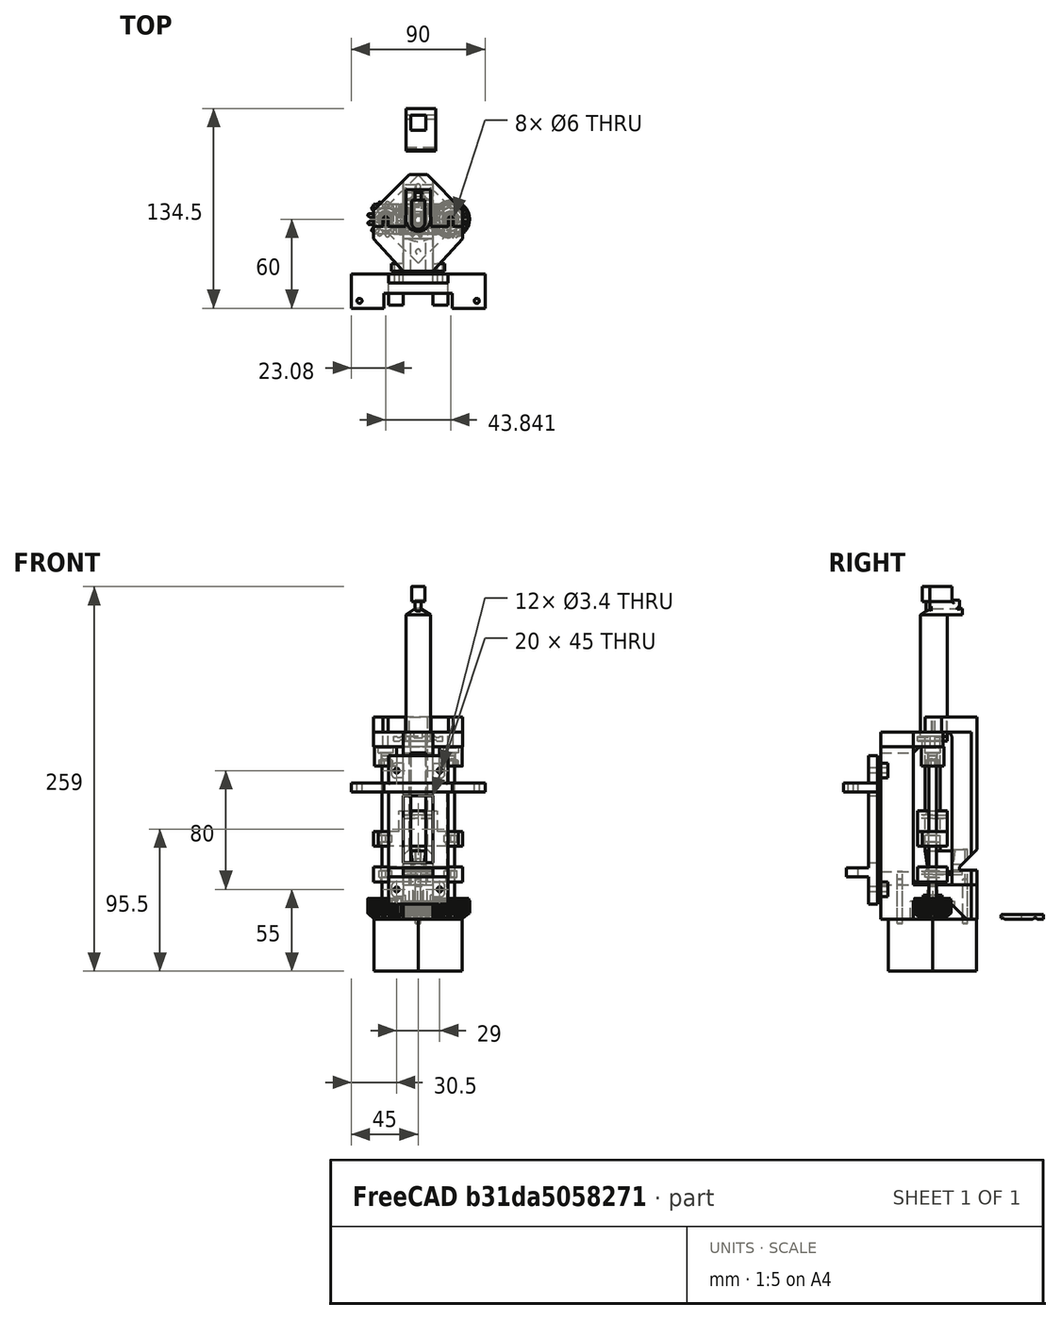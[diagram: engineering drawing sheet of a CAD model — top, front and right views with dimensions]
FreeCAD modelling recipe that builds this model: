
FCSTD DOCUMENT  (FreeCAD 0.19R24291 (Git))
Label: syringe-pump
License: CC-BY 3.0
LicenseURL: http://creativecommons.org/licenses/by/3.0/
objects: Part::Cut×65, Part::Box×55, Part::Cylinder×53, Part::Fuse×40, Part::Fillet×20, Part::Chamfer×9, Part::Feature×8, Part::MultiCommon×7, App::DocumentObjectGroup×6, Part::MultiFuse×5, Part::Cone×4, Part::FeaturePython×4, Part::Wedge×3
note: 273 computed .brp shape members not serialized (recipe doc carries the construction recipe); baked Part::Feature solids carry a one-line shape summary decoded from their .brp

FEATURE [Part::Cylinder] Cylinder
  Angle = 360
  AttacherType = Attacher::AttachEngine3D
  Height = 22
  Radius = 2.6
FEATURE [Part::Box] Box  label="Cube"
  AttacherType = Attacher::AttachEngine3D
  Height = 30
  Length = 10
  Placement = pos=(-5,2,-1) rot=(0,0,1;0rad)
  Width = 10
FEATURE [Part::Cut] Cut  label="motor-shaft"
  Base = -> Cylinder
  Placement = pos=(0,0,0) rot=(0,0,1;0.785398rad)
  Tool = -> Box
FEATURE [Part::Cylinder] Cylinder001  label="screw1"
  Angle = 360
  AttacherType = Attacher::AttachEngine3D
  Height = 30
  Placement = pos=(-1e-15,21.9203,-3) rot=(0,0,1;0.785398rad)
  Radius = 1.7
FEATURE [Part::Cylinder] Cylinder002  label="drive-screw-2"
  Angle = 360
  AttacherType = Attacher::AttachEngine3D
  Height = 100
  Placement = pos=(-21.9203,-1e-15,10) rot=(0,0,1;0.785398rad)
  Radius = 2.5
FEATURE [Part::Cylinder] Cylinder003  label="screw3"
  Angle = 360
  AttacherType = Attacher::AttachEngine3D
  Height = 30
  Placement = pos=(1e-15,-21.9203,-3) rot=(0,0,1;0.785398rad)
  Radius = 1.7
FEATURE [Part::Cylinder] Cylinder004  label="drive-screw-1"
  Angle = 360
  AttacherType = Attacher::AttachEngine3D
  Height = 100
  Placement = pos=(21.9203,1e-15,10) rot=(0,0,1;0.785398rad)
  Radius = 2.5
FEATURE [Part::Feature] Part__Feature  label="paste-extruder-drive-gear-a"
  Placement = pos=(0,0,3) rot=(0,0,1;0rad)
  shape: bbox 24.94 x 25.13 x 8 mm, 389 faces (baked)
FEATURE [Part::Cylinder] Cylinder005  label="Cylinder001"
  Angle = 360
  AttacherType = Attacher::AttachEngine3D
  Height = 85
  Radius = 8.25
FEATURE [Part::Box] Box001  label="Cube001"
  AttacherType = Attacher::AttachEngine3D
  Height = 3
  Length = 20
  Placement = pos=(-8.25,-16.5,0) rot=(0,0,1;0rad)
  Width = 33
FEATURE [Part::Cone] Cone
  Angle = 360
  AttacherType = Attacher::AttachEngine3D
  Height = 4
  Placement = pos=(0,0,85) rot=(0,0,1;0rad)
  Radius1 = 8.25
  Radius2 = 2
FEATURE [Part::Cylinder] Cylinder006  label="Cylinder002"
  Angle = 360
  AttacherType = Attacher::AttachEngine3D
  Height = 10
  Placement = pos=(-2.3,0,94) rot=(0,0,1;0rad)
  Radius = 4.5
FEATURE [Part::Cylinder] Cylinder007  label="Cylinder003"
  Angle = 360
  AttacherType = Attacher::AttachEngine3D
  Height = 10
  Placement = pos=(-2.3,0,85) rot=(0,0,1;0rad)
  Radius = 2
FEATURE [Part::Cylinder] Cylinder008  label="Cylinder004"
  Angle = 360
  AttacherType = Attacher::AttachEngine3D
  Height = 24
  Placement = pos=(-10,11,-1.3) rot=(0,1,0;1.5708rad)
  Radius = 2
FEATURE [Part::Cylinder] Cylinder009  label="Cylinder005"
  Angle = 360
  AttacherType = Attacher::AttachEngine3D
  Height = 24
  Placement = pos=(-10,-11,-1.3) rot=(0,1,0;1.5708rad)
  Radius = 2
FEATURE [Part::Cylinder] Cylinder010  label="Cylinder006"
  Angle = 360
  AttacherType = Attacher::AttachEngine3D
  Height = 24
  Placement = pos=(-10,13,4.3) rot=(0,1,0;1.5708rad)
  Radius = 2
FEATURE [Part::Cylinder] Cylinder011  label="Cylinder007"
  Angle = 360
  AttacherType = Attacher::AttachEngine3D
  Height = 24
  Placement = pos=(-10,-13,4.3) rot=(0,1,0;1.5708rad)
  Radius = 2
FEATURE [Part::Cut] Cut001
  Base = -> Box001
  Tool = -> Cylinder008
FEATURE [Part::Cut] Cut002
  Base = -> Cut001
  Tool = -> Cylinder009
FEATURE [Part::Cut] Cut003
  Base = -> Cut002
  Tool = -> Cylinder011
FEATURE [Part::Cut] Cut004
  Base = -> Cut003
  Placement = pos=(-2,0,0) rot=(0,0,1;0rad)
  Tool = -> Cylinder010
FEATURE [Part::Fuse] Fusion
  Base = -> Cylinder005
  Tool = -> Cut004
FEATURE [Part::Fuse] Fusion001
  Base = -> Cylinder007
  Tool = -> Fusion
FEATURE [Part::Fuse] Fusion002  label="syringe-1"
  Base = -> Cylinder006
  Tool = -> Fusion001
FEATURE [Part::Fuse] Fusion003
  Base = -> Cone
  Tool = -> Fusion002
FEATURE [Part::Box] Box002  label="Cube002"
  AttacherType = Attacher::AttachEngine3D
  Height = 80
  Length = 10
  Placement = pos=(-5,-5,16) rot=(0,0,1;0rad)
  Width = 10
FEATURE [Part::Wedge] Wedge
  AttacherType = Attacher::AttachEngine3D
  Placement = pos=(-5,-5,16) rot=(-1,0,0;1.5708rad)
  X2max = 18
  X2min = 2
  Xmax = 20
  Xmin = 0
  Ymax = 14
  Ymin = 0
  Z2max = 8
  Z2min = 2
  Zmax = 10
  Zmin = 0
FEATURE [Part::Cylinder] Cylinder012  label="Cylinder008"
  Angle = 360
  AttacherType = Attacher::AttachEngine3D
  Height = 2
  Radius = 9.5
FEATURE [Part::Fuse] Fusion004
  Base = -> Box002
  Tool = -> Wedge
FEATURE [Part::Fuse] Fusion005
  Base = -> Cylinder012
  Tool = -> Fusion004
FEATURE [Part::Box] Box003  label="motor-body"
  AttacherType = Attacher::AttachEngine3D
  Height = 35
  Length = 42
  Placement = pos=(2e-15,-29.6985,-35) rot=(0,0,1;0.785398rad)
  Width = 42
FEATURE [Part::Box] Box004  label="Cube003"
  AttacherType = Attacher::AttachEngine3D
  Height = 2
  Length = 20
  Placement = pos=(0,-9.5,0) rot=(0,0,1;0rad)
  Width = 19
FEATURE [Part::Fuse] Fusion006
  Base = -> Fusion005
  Tool = -> Box004
FEATURE [Part::Fillet] Fillet001
  Base = -> Fusion006
  Edges = 3 edges r=3: [Edge9,Edge20,Edge24]
FEATURE [Part::Fillet] Fillet002
  Base = -> Fillet001
  Edges = 3 edges r=3: [Edge8,Edge27,Edge29]
FEATURE [Part::Fillet] Fillet003  label="piston"
  Base = -> Fillet002
  Edges = 3 edges r=3: [Edge33,Edge34,Edge36]
  Placement = pos=(0,0,30) rot=(0,0,1;0.785398rad)
FEATURE [Part::Box] Box005  label="Cube004"
  AttacherType = Attacher::AttachEngine3D
  Height = 85
  Length = 10
  Placement = pos=(0,-8.25,0) rot=(0,0,1;0rad)
  Width = 16.5
FEATURE [Part::Fuse] Fusion007
  Base = -> Fusion003
  Tool = -> Box005
FEATURE [Part::Wedge] Wedge003
  AttacherType = Attacher::AttachEngine3D
  Placement = pos=(0,8.25,85) rot=(1,0,0;1.5708rad)
  X2max = 20
  X2min = 0
  Xmax = 20
  Xmin = 0
  Ymax = 4
  Ymin = 0
  Z2max = 10.25
  Z2min = 6.25
  Zmax = 16.5
  Zmin = 0
FEATURE [Part::Fuse] Fusion008
  Base = -> Fusion007
  Tool = -> Wedge003
FEATURE [Part::Box] Box006  label="Cube005"
  AttacherType = Attacher::AttachEngine3D
  Height = 10
  Length = 20
  Placement = pos=(-2,-2,85) rot=(0,0,1;0rad)
  Width = 4
FEATURE [Part::Fuse] Fusion009
  Base = -> Fusion008
  Tool = -> Box006
FEATURE [Part::Box] Box007  label="Cube006"
  AttacherType = Attacher::AttachEngine3D
  Height = 10
  Length = 15
  Placement = pos=(-2,-4.5,94) rot=(0,0,1;0rad)
  Width = 9
FEATURE [Part::Fuse] Fusion010
  Base = -> Fusion009
  Tool = -> Box007
FEATURE [Part::Fillet] Fillet  label="syringe-body"
  Base = -> Fusion010
  Edges = 5 edges r=1.5: [Edge23,Edge27,Edge33,Edge38,Edge58]
  Placement = pos=(0,0,120) rot=(0,0,1;1.5708rad)
FEATURE [Part::Box] Box008  label="Cube007"
  AttacherType = Attacher::AttachEngine3D
  Height = 10
  Length = 20
  Placement = pos=(14.1421,-28.2843,25) rot=(0,0,1;0.785398rad)
  Width = 60
FEATURE [Part::Cut] Cut005
  Base = -> Box008
  Tool = -> Fillet003
FEATURE [Part::Fillet] Fillet004
  Base = -> Fillet001
  Edges = 3 edges r=3: [Edge8,Edge27,Edge29]
FEATURE [Part::Fillet] Fillet005  label="piston001"
  Base = -> Fillet004
  Edges = 3 edges r=3: [Edge33,Edge34,Edge36]
  Placement = pos=(0,0,30) rot=(0,0,1;1.5708rad)
FEATURE [App::DocumentObjectGroup] Group001  label="syringe"
  Group = -> [Fillet003,Fillet,Fillet005]
FEATURE [Part::Cylinder] Cylinder017  label="drive-screw-003"
  Angle = 360
  AttacherType = Attacher::AttachEngine3D
  Height = 100
  Placement = pos=(15.5,-15.5,10) rot=(0,0,1;0rad)
  Radius = 3
FEATURE [Part::Cylinder] Cylinder018  label="drive-screw-004"
  Angle = 360
  AttacherType = Attacher::AttachEngine3D
  Height = 100
  Placement = pos=(-15.5,15.5,10) rot=(0,0,1;0rad)
  Radius = 3
FEATURE [Part::Cut] Cut006
  Base = -> Cut005
  Tool = -> Cylinder017
FEATURE [Part::Cut] Cut007
  Base = -> Cut006
  Tool = -> Cylinder018
FEATURE [Part::Box] Box009  label="Cube008"
  AttacherType = Attacher::AttachEngine3D
  Height = 4.5
  Length = 20
  Placement = pos=(0,-4.25,0) rot=(0,0,1;0rad)
  Width = 8.5
FEATURE [Part::Box] Box010  label="Cube009"
  AttacherType = Attacher::AttachEngine3D
  Height = 8
  Length = 20
  Placement = pos=(0,0,-1) rot=(0,0,1;1.0472rad)
  Width = 8.5
FEATURE [Part::Box] Box011  label="Cube010"
  AttacherType = Attacher::AttachEngine3D
  Height = 8
  Length = 20
  Placement = pos=(0,0,-1) rot=(0,0,1;3.66519rad)
  Width = 8.5
FEATURE [Part::Cut] Cut008
  Base = -> Box009
  Tool = -> Box010
FEATURE [Part::Cut] Cut009
  Base = -> Cut008
  Placement = pos=(11.965,-19.035,28) rot=(0,0,1;0.785398rad)
  Tool = -> Box011
FEATURE [Part::Box] Box012  label="Cube011"
  AttacherType = Attacher::AttachEngine3D
  Height = 8
  Length = 20
  Placement = pos=(0,0,-1) rot=(0,0,1;3.66519rad)
  Width = 8.5
FEATURE [Part::Cut] Cut011
  Base = -> Box009
  Tool = -> Box010
FEATURE [Part::Cut] Cut010
  Base = -> Cut011
  Placement = pos=(-19.035,11.965,28) rot=(0,0,1;0.785398rad)
  Tool = -> Box012
FEATURE [Part::Cut] Cut012
  Base = -> Cut007
  Tool = -> Cut009
FEATURE [Part::Cut] Cut013  label="paste-extruder-drive-blockaa"
  Base = -> Cut012
  Placement = pos=(0,0,0) rot=(0,0,1;0.785398rad)
  Tool = -> Cut010
FEATURE [Part::Feature] Part__Feature001  label="paste-extruder-driven-gear-a"
  Placement = pos=(21.9203,0,3) rot=(0,0,1;0rad)
  shape: bbox 25.3 x 25.3 x 13 mm, 290 faces (baked)
FEATURE [Part::Feature] Part__Feature003  label="Z Driven Gear002"
  shape: bbox 25.3 x 25.3 x 13 mm, 290 faces (baked)
FEATURE [Part::Cylinder] Cylinder019  label="Cylinder009"
  Angle = 360
  AttacherType = Attacher::AttachEngine3D
  Height = 20
  Placement = pos=(0,0,-4) rot=(0,0,1;0rad)
  Radius = 7.5
FEATURE [Part::MultiCommon] Common  label="paste-extruder-bearing-holder-a"
  Placement = pos=(21.9203,1e-15,113) rot=(0.92388,0.382683,0;3.14159rad)
  Shapes = -> [Part__Feature003,Cylinder019]
FEATURE [Part::Feature] Part__Feature004  label="Z Driven Gear003"
  shape: bbox 25.3 x 25.3 x 13 mm, 290 faces (baked)
FEATURE [Part::Cylinder] Cylinder020  label="Cylinder010"
  Angle = 360
  AttacherType = Attacher::AttachEngine3D
  Height = 20
  Placement = pos=(0,0,-4) rot=(0,0,1;0rad)
  Radius = 7.5
FEATURE [Part::MultiCommon] Common001  label="paste-extruder-bearing-holder-b"
  Placement = pos=(-21.9203,-1e-15,113) rot=(0.92388,0.382683,0;3.14159rad)
  Shapes = -> [Part__Feature004,Cylinder020]
FEATURE [App::DocumentObjectGroup] Group002  label="Hardware"
  Group = -> [Box003,Cylinder003,Cylinder001,Cylinder004,Cylinder002,Cut]
FEATURE [Part::Box] Box013  label="Cube012"
  AttacherType = Attacher::AttachEngine3D
  Height = 10
  Length = 20
  Placement = pos=(30,-13,116) rot=(0,0,1;1.5708rad)
  Width = 60
FEATURE [Part::Box] Box014  label="Cube013"
  AttacherType = Attacher::AttachEngine3D
  Height = 146
  Length = 20
  Placement = pos=(-10,-35,-20) rot=(0,0,1;0rad)
  Width = 22
FEATURE [Part::Cylinder] Cylinder021  label="Cylinder011"
  Angle = 360
  AttacherType = Attacher::AttachEngine3D
  Height = 12
  Radius = 15
FEATURE [Part::Box] Box016  label="motor-body001"
  AttacherType = Attacher::AttachEngine3D
  Height = 35
  Length = 82
  Placement = pos=(0,-49.6985,-35) rot=(0,0,1;0.785398rad)
  Width = 82
FEATURE [Part::Cylinder] Cylinder022  label="screw004"
  Angle = 360
  AttacherType = Attacher::AttachEngine3D
  Height = 60
  Placement = pos=(0,-21.9203,-3) rot=(0,0,1;0.785398rad)
  Radius = 1.7
FEATURE [Part::Box] Box017  label="Cube015"
  AttacherType = Attacher::AttachEngine3D
  Height = 10
  Length = 20
  Placement = pos=(-10,-35,116) rot=(0,0,1;0.737402rad)
  Width = 29.74
FEATURE [Part::Box] Box018  label="Cube016"
  AttacherType = Attacher::AttachEngine3D
  Height = 10
  Length = 29.74
  Placement = pos=(10,-35,116) rot=(0,0,1;0.833395rad)
  Width = 20
FEATURE [Part::Fuse] Fusion014
  Base = -> Fusion009
  Tool = -> Box007
FEATURE [Part::Fillet] Fillet006  label="syringe-body001"
  Base = -> Fusion014
  Edges = 5 edges r=1.5: [Edge23,Edge27,Edge33,Edge38,Edge58]
  Placement = pos=(0,0,120) rot=(0,0,1;1.5708rad)
FEATURE [Part::Box] Box019  label="Cube017"
  AttacherType = Attacher::AttachEngine3D
  Height = 10
  Length = 12
  Placement = pos=(-6,-7,111) rot=(0,0,1;0rad)
  Width = 20
FEATURE [Part::Cylinder] Cylinder023  label="drive-screw-005"
  Angle = 360
  AttacherType = Attacher::AttachEngine3D
  Height = 100
  Placement = pos=(21.9203,0,50) rot=(0,0,1;0.785398rad)
  Radius = 1.7
FEATURE [Part::Cylinder] Cylinder024  label="drive-screw-006"
  Angle = 360
  AttacherType = Attacher::AttachEngine3D
  Height = 100
  Placement = pos=(-21.9203,0,50) rot=(0,0,1;0.785398rad)
  Radius = 1.7
FEATURE [Part::Box] Box020  label="Cube018"
  AttacherType = Attacher::AttachEngine3D
  Height = 10
  Length = 10
  Placement = pos=(8,-35,15) rot=(0,0,1;0rad)
  Width = 5
FEATURE [Part::Cylinder] Cylinder025  label="Cylinder012"
  Angle = 360
  AttacherType = Attacher::AttachEngine3D
  Height = 50
  Placement = pos=(14.5,-15,20) rot=(1,0,0;1.5708rad)
  Radius = 1.7
FEATURE [Part::Cut] Cut022
  Base = -> Box020
  Tool = -> Cylinder025
FEATURE [Part::Fillet] Fillet007
  Base = -> Cut022
  Edges = 1 edges r=3: [Edge14]
FEATURE [Part::Fillet] Fillet008  label="tab"
  Base = -> Fillet007
  Edges = 1 edges r=3: [Edge14]
FEATURE [Part::Fillet] Fillet009
  Base = -> Cut022
  Edges = 1 edges r=3: [Edge14]
FEATURE [Part::Fillet] Fillet010  label="tab001"
  Base = -> Fillet009
  Edges = 1 edges r=3: [Edge14]
  Placement = pos=(0,0,80) rot=(0,0,1;0rad)
FEATURE [Part::Fillet] Fillet011
  Base = -> Cut022
  Edges = 1 edges r=3: [Edge14]
FEATURE [Part::Fillet] Fillet012  label="tab002"
  Base = -> Fillet011
  Edges = 1 edges r=3: [Edge14]
  Placement = pos=(0,0,40) rot=(0,1,0;3.14159rad)
FEATURE [Part::Fillet] Fillet013
  Base = -> Cut022
  Edges = 1 edges r=3: [Edge14]
FEATURE [Part::Fillet] Fillet014  label="tab003"
  Base = -> Fillet013
  Edges = 1 edges r=3: [Edge14]
  Placement = pos=(0,0,120) rot=(0,1,0;3.14159rad)
FEATURE [Part::Box] Box021  label="body-slot"
  AttacherType = Attacher::AttachEngine3D
  Height = 89
  Length = 10
  Placement = pos=(-5,-40,23) rot=(0,0,1;0rad)
  Width = 80
FEATURE [Part::Box] Box022  label="Cube019"
  AttacherType = Attacher::AttachEngine3D
  Height = 23
  Length = 20
  Placement = pos=(-10,-35,0) rot=(0,0,1;0rad)
  Width = 65
FEATURE [Part::Box] Box023  label="Cube020"
  AttacherType = Attacher::AttachEngine3D
  Height = 20
  Length = 30
  Placement = pos=(-15,10,13) rot=(-1,0,0;0.785398rad)
  Width = 65
FEATURE [Part::Box] Box024  label="Cube021"
  AttacherType = Attacher::AttachEngine3D
  Height = 20
  Length = 30
  Placement = pos=(-15,-37,12) rot=(0,0,1;0rad)
  Width = 70
FEATURE [Part::Fuse] Fusion015
  Base = -> Box023
  Tool = -> Box024
FEATURE [Part::MultiCommon] Common002
  Shapes = -> [Box022,Fusion015]
FEATURE [Part::Fuse] Fusion016
  Base = -> Box014
  Tool = -> Common002
FEATURE [Part::Chamfer] Chamfer
  Base = -> Fusion016
  Edges = 1 edges r=4: [Edge27]
FEATURE [Part::Chamfer] Chamfer001
  Base = -> Chamfer
  Edges = 1 edges r=4: [Edge26]
FEATURE [Part::Cut] Cut023
  Base = -> Chamfer001
  Tool = -> Cylinder021
FEATURE [Part::Cut] Cut024
  Base = -> Cut023
  Tool = -> Cylinder022
FEATURE [Part::Cut] Cut025
  Base = -> Cut024
  Tool = -> Box016
FEATURE [Part::Cylinder] Cylinder026  label="screw005"
  Angle = 360
  AttacherType = Attacher::AttachEngine3D
  Height = 56
  Placement = pos=(0,21.9203,-3) rot=(0,0,1;0.785398rad)
  Radius = 1.7
FEATURE [Part::Cut] Cut026
  Base = -> Cut025
  Tool = -> Cylinder026
FEATURE [Part::Fuse] Fusion017
  Base = -> Box013
  Tool = -> Box018
FEATURE [Part::Fuse] Fusion018
  Base = -> Box017
  Tool = -> Fusion017
FEATURE [Part::Fuse] Fusion019
  Base = -> Cut026
  Tool = -> Fusion018
FEATURE [Part::Fuse] Fusion020
  Base = -> Fillet008
  Tool = -> Fusion019
FEATURE [Part::Fuse] Fusion021
  Base = -> Fillet014
  Tool = -> Fusion020
FEATURE [Part::Fuse] Fusion022
  Base = -> Fillet012
  Tool = -> Fusion021
FEATURE [Part::Fuse] Fusion023
  Base = -> Fillet010
  Tool = -> Fusion022
FEATURE [Part::Cut] Cut027
  Base = -> Fusion023
  Tool = -> Fillet006
FEATURE [Part::Cut] Cut028
  Base = -> Cut027
  Tool = -> Box019
FEATURE [Part::Cut] Cut029
  Base = -> Cut028
  Tool = -> Cylinder024
FEATURE [Part::Cut] Cut030
  Base = -> Cut029
  Tool = -> Cylinder023
FEATURE [Part::Cut] Cut031
  Base = -> Cut030
  Tool = -> Box021
FEATURE [Part::Cylinder] Cylinder027  label="drive-screw-007"
  Angle = 360
  AttacherType = Attacher::AttachEngine3D
  Height = 10
  Placement = pos=(21.9203,0,6) rot=(0,0,1;0.785398rad)
  Radius = 13.5
FEATURE [Part::Cylinder] Cylinder028  label="drive-screw-008"
  Angle = 360
  AttacherType = Attacher::AttachEngine3D
  Height = 10
  Placement = pos=(-21.9203,0,6) rot=(0,0,1;0.785398rad)
  Radius = 13.5
FEATURE [Part::Cut] Cut032
  Base = -> Cut031
  Tool = -> Cylinder027
FEATURE [Part::Cut] Cut033  label="frame-1"
  Base = -> Cut032
  Tool = -> Cylinder028
FEATURE [Part::Cylinder] Cylinder029  label="Cylinder013"
  Angle = 360
  AttacherType = Attacher::AttachEngine3D
  Height = 50
  Radius = 3.5
FEATURE [Part::Cut] Cut034  label="old-frame"
  Base = -> Cut033
  Tool = -> Cylinder029
FEATURE [Part::FeaturePython] Clone  label="paste-extruder-bearing-holder-1"  # Draft clone (typed FeaturePython)
  Objects = -> [Common]
  Placement = pos=(21.3,0,113) rot=(0.92388,0.382683,0;3.14159rad)
  Scale = (1.03,1.03,1)
FEATURE [Part::Cylinder] Cylinder030  label="mounting hole"
  Angle = 360
  AttacherType = Attacher::AttachEngine3D
  Height = 50
  Placement = pos=(-14.5,0,20) rot=(1,0,0;1.5708rad)
  Radius = 1.7
FEATURE [Part::Cylinder] Cylinder031  label="mounting hole001"
  Angle = 360
  AttacherType = Attacher::AttachEngine3D
  Height = 50
  Placement = pos=(14.5,0,20) rot=(1,0,0;1.5708rad)
  Radius = 1.7
FEATURE [Part::Cylinder] Cylinder032  label="mounting hole002"
  Angle = 360
  AttacherType = Attacher::AttachEngine3D
  Height = 50
  Placement = pos=(-14.5,0,100) rot=(1,0,0;1.5708rad)
  Radius = 1.7
FEATURE [Part::Cylinder] Cylinder033  label="mounting hole003"
  Angle = 360
  AttacherType = Attacher::AttachEngine3D
  Height = 50
  Placement = pos=(14.5,0,100) rot=(1,0,0;1.5708rad)
  Radius = 1.7
FEATURE [Part::Box] Box025  label="Cube022"
  AttacherType = Attacher::AttachEngine3D
  Height = 100
  Length = 40
  Placement = pos=(-20,-41,10) rot=(0,0,1;0rad)
  Width = 6
FEATURE [Part::Box] Box026  label="Cube023"
  AttacherType = Attacher::AttachEngine3D
  Height = 6
  Length = 90
  Placement = pos=(-45,-58,85.5) rot=(0,0,1;0rad)
  Width = 23
FEATURE [Part::Box] Box027  label="Cube024"
  AttacherType = Attacher::AttachEngine3D
  Height = 6
  Length = 40
  Placement = pos=(-20,-56,28.5) rot=(0,0,1;0rad)
  Width = 15
FEATURE [Part::Cylinder] Cylinder034  label="mounting hole004"
  Angle = 360
  AttacherType = Attacher::AttachEngine3D
  Height = 50
  Placement = pos=(-39.5,-53,58) rot=(0,0,1;0rad)
  Radius = 1.7
FEATURE [Part::Cylinder] Cylinder035  label="mounting hole005"
  Angle = 360
  AttacherType = Attacher::AttachEngine3D
  Height = 50
  Placement = pos=(39.5,-53,58) rot=(0,0,1;0rad)
  Radius = 1.7
FEATURE [Part::Box] Box028  label="Cube025"
  AttacherType = Attacher::AttachEngine3D
  Height = 45
  Length = 20
  Placement = pos=(-10,-51,38) rot=(0,0,1;0rad)
  Width = 20
FEATURE [Part::Box] Box029  label="Cube026"
  AttacherType = Attacher::AttachEngine3D
  Height = 45
  Length = 20
  Placement = pos=(-10,-68,20) rot=(0,0,1;0rad)
  Width = 20
FEATURE [Part::Box] Box030  label="Cube027"
  AttacherType = Attacher::AttachEngine3D
  Height = 45
  Length = 46
  Placement = pos=(-23,-68,56) rot=(0,0,1;0rad)
  Width = 20
FEATURE [Part::Fuse] Fusion024
  Base = -> Box025
  Tool = -> Box026
FEATURE [Part::Fuse] Fusion025
  Base = -> Box027
  Tool = -> Fusion024
FEATURE [Part::Cut] Cut035
  Base = -> Fusion025
  Tool = -> Cylinder035
FEATURE [Part::Cut] Cut036
  Base = -> Cut035
  Tool = -> Cylinder034
FEATURE [Part::Cut] Cut037
  Base = -> Cut036
  Tool = -> Cylinder033
FEATURE [Part::Cut] Cut038
  Base = -> Cut037
  Tool = -> Cylinder032
FEATURE [Part::Cut] Cut039
  Base = -> Cut038
  Tool = -> Cylinder031
FEATURE [Part::Cut] Cut040
  Base = -> Cut039
  Tool = -> Cylinder030
FEATURE [Part::Cut] Cut041
  Base = -> Cut040
  Tool = -> Box030
FEATURE [Part::Cut] Cut042
  Base = -> Cut041
  Tool = -> Box029
FEATURE [Part::Cut] Cut043  label="paste-extruder-PSU-mounting-bracket"
  Base = -> Cut042
  Placement = pos=(0,-2,0) rot=(0,0,1;0rad)
  Tool = -> Box028
FEATURE [Part::Cylinder] Cylinder036  label="drive-screw-009"
  Angle = 360
  AttacherType = Attacher::AttachEngine3D
  Height = 100
  Placement = pos=(21.9203,0,50) rot=(0,0,1;0.785398rad)
  Radius = 1.7
FEATURE [Part::Cut] Cut044
  Base = -> Cut028
  Tool = -> Cylinder024
FEATURE [Part::Cut] Cut045
  Base = -> Cut044
  Tool = -> Cylinder036
FEATURE [Part::Box] Box031  label="body-slot001"
  AttacherType = Attacher::AttachEngine3D
  Height = 80
  Length = 10
  Placement = pos=(-5,-40,32) rot=(0,0,1;0rad)
  Width = 80
FEATURE [Part::Cylinder] Cylinder037  label="drive-screw-010"
  Angle = 360
  AttacherType = Attacher::AttachEngine3D
  Height = 10
  Placement = pos=(21.9203,0,6) rot=(0,0,1;0.785398rad)
  Radius = 13.5
FEATURE [Part::Cylinder] Cylinder038  label="drive-screw-011"
  Angle = 360
  AttacherType = Attacher::AttachEngine3D
  Height = 10
  Placement = pos=(-21.9203,0,6) rot=(0,0,1;0.785398rad)
  Radius = 13.5
FEATURE [Part::Cylinder] Cylinder039  label="Cylinder014"
  Angle = 360
  AttacherType = Attacher::AttachEngine3D
  Height = 50
  Radius = 3.5
FEATURE [Part::Fillet] Fillet015
  Base = -> Cut045
  Edges = 1 edges r=5: [Edge51]
FEATURE [Part::Cut] Cut046
  Base = -> Fillet015
  Tool = -> Box031
FEATURE [Part::Box] Box032  label="Cube028"
  AttacherType = Attacher::AttachEngine3D
  Height = 6
  Length = 20
  Placement = pos=(-10,-13,112) rot=(1,0,0;0.785398rad)
  Width = 6
FEATURE [Part::Fuse] Fusion026
  Base = -> Cut046
  Tool = -> Box032
FEATURE [Part::Cut] Cut047
  Base = -> Fusion026
  Tool = -> Cylinder039
FEATURE [Part::Cut] Cut048
  Base = -> Cut047
  Tool = -> Cylinder038
FEATURE [Part::Cut] Cut049  label="paste-extruder-frame"
  Base = -> Cut048
  Tool = -> Cylinder037
FEATURE [Part::Box] Box033  label="Cube029"
  AttacherType = Attacher::AttachEngine3D
  Height = 103
  Length = 20
  Placement = pos=(-10,13,23) rot=(0,0,1;0rad)
  Width = 17
FEATURE [Part::Box] Box034  label="Cube030"
  AttacherType = Attacher::AttachEngine3D
  Height = 10
  Length = 60
  Placement = pos=(-30,-5,126) rot=(0,0,1;0rad)
  Width = 35
FEATURE [Part::Box] Box035  label="Cube031"
  AttacherType = Attacher::AttachEngine3D
  Height = 122
  Length = 41
  Placement = pos=(-31,5,19) rot=(0,0,1;0.785398rad)
  Width = 17
FEATURE [Part::Box] Box036  label="Cube032"
  AttacherType = Attacher::AttachEngine3D
  Height = 124
  Length = 20
  Placement = pos=(33,3,19) rot=(0,0,1;0.785398rad)
  Width = 42
FEATURE [Part::Fuse] Fusion027
  Base = -> Box033
  Tool = -> Box034
FEATURE [Part::Cut] Cut050
  Base = -> Fusion027
  Tool = -> Box036
FEATURE [Part::Cut] Cut051
  Base = -> Cut050
  Tool = -> Box035
FEATURE [Part::Cylinder] Cylinder040  label="screw006"
  Angle = 360
  AttacherType = Attacher::AttachEngine3D
  Height = 56
  Placement = pos=(0,21.9203,-3) rot=(0,0,1;0.785398rad)
  Radius = 1.7
FEATURE [Part::Cylinder] Cylinder041  label="drive-screw-012"
  Angle = 360
  AttacherType = Attacher::AttachEngine3D
  Height = 100
  Placement = pos=(-21.9203,0,50) rot=(0,0,1;0.785398rad)
  Radius = 1.7
FEATURE [Part::Cylinder] Cylinder042  label="drive-screw-013"
  Angle = 360
  AttacherType = Attacher::AttachEngine3D
  Height = 100
  Placement = pos=(21.9203,0,50) rot=(0,0,1;0.785398rad)
  Radius = 1.7
FEATURE [Part::Box] Box037  label="Cube033"
  AttacherType = Attacher::AttachEngine3D
  Height = 56
  Length = 3.4
  Placement = pos=(-1.7,-2,-3) rot=(0,0,1;0rad)
  Width = 24
FEATURE [Part::Box] Box038  label="Cube034"
  AttacherType = Attacher::AttachEngine3D
  Height = 100
  Length = 3.4
  Placement = pos=(-23.7,-24,50) rot=(0,0,1;0rad)
  Width = 24
FEATURE [Part::Fuse] Fusion028  label="top-slot"
  Base = -> Cylinder040
  Placement = pos=(0,0,-6) rot=(0,0,1;0rad)
  Tool = -> Box037
FEATURE [Part::Box] Box039  label="Cube035"
  AttacherType = Attacher::AttachEngine3D
  Height = 100
  Length = 3.4
  Placement = pos=(20.3,-24,50) rot=(0,0,1;0rad)
  Width = 24
FEATURE [Part::Fuse] Fusion029  label="bottom-slot-1"
  Base = -> Cylinder042
  Tool = -> Box039
FEATURE [Part::Fuse] Fusion030  label="bottom-slot-2"
  Base = -> Cylinder041
  Tool = -> Box038
FEATURE [Part::Box] Box040  label="Cube036"
  AttacherType = Attacher::AttachEngine3D
  Height = 16
  Length = 22
  Placement = pos=(-11,18,33) rot=(0,0,1;0rad)
  Width = 17
FEATURE [Part::Box] Box041  label="Cube037"
  AttacherType = Attacher::AttachEngine3D
  Height = 16
  Length = 25
  Placement = pos=(-13,18,35) rot=(1,0,0;0.785398rad)
  Width = 32
FEATURE [Part::Cut] Cut052
  Base = -> Box040
  Tool = -> Box041
FEATURE [Part::Cut] Cut053
  Base = -> Cut051
  Tool = -> Cut052
FEATURE [Part::Cut] Cut054
  Base = -> Cut053
  Tool = -> Fusion028
FEATURE [Part::Cut] Cut055
  Base = -> Cut054
  Tool = -> Fusion030
FEATURE [Part::Cut] Cut056  label="top-strengthener1"
  Base = -> Cut055
  Tool = -> Fusion029
FEATURE [Part::Box] Box042  label="Cube038"
  AttacherType = Attacher::AttachEngine3D
  Height = 18
  Length = 17
  Placement = pos=(-8.5,-7,125) rot=(0,0,1;0rad)
  Width = 17
FEATURE [Part::Cylinder] Cylinder043  label="Cylinder015"
  Angle = 360
  AttacherType = Attacher::AttachEngine3D
  Height = 36
  Placement = pos=(0,10,121) rot=(0,0,1;0rad)
  Radius = 8.5
FEATURE [Part::Fuse] Fusion031
  Base = -> Box042
  Placement = pos=(0,-9,0) rot=(0,0,1;0rad)
  Tool = -> Cylinder043
FEATURE [Part::Cut] Cut057  label="top-strengthener2"
  Base = -> Cut056
  Tool = -> Fusion031
FEATURE [Part::Box] Box043  label="Cube039"
  AttacherType = Attacher::AttachEngine3D
  Height = 4
  Length = 7.5
  Placement = pos=(-3.75,11,33) rot=(0,0,1;0rad)
  Width = 27
FEATURE [Part::Cut] Cut058  label="top-strengthener3"
  Base = -> Cut057
  Tool = -> Box043
FEATURE [Part::Fillet] Fillet016  label="paste-extruder-top-strengthener"
  Base = -> Cut058
  Edges = 1 edges r=4: [Edge40]
FEATURE [Part::MultiCommon] Common003  label="paste-extruder-bearing-holder-2"
  Placement = pos=(-21.9,0,113) rot=(0.92388,0.382683,0;3.14159rad)
  Shapes = -> [Part__Feature003,Cylinder019]
FEATURE [Part::Cut] Cut060
  Base = -> Cut011
  Placement = pos=(-19.035,11.965,28) rot=(0,0,1;0.785398rad)
  Tool = -> Box012
FEATURE [Part::Cut] Cut061
  Base = -> Cut007
  Tool = -> Cut009
FEATURE [Part::Cut] Cut059  label="paste-extruder-drive-block001"
  Base = -> Cut061
  Placement = pos=(0,0,61) rot=(0,0,1;0.785398rad)
  Tool = -> Cut060
FEATURE [Part::Box] Box044  label="Cube040"
  AttacherType = Attacher::AttachEngine3D
  Height = 30
  Length = 50
  Placement = pos=(-25,-32,-1) rot=(0,0,1;0rad)
  Width = 20
FEATURE [Part::Cut] Cut063
  Base = -> Cut003
  Tool = -> Box
FEATURE [Part::Cut] Cut062  label="paste-extruder-charger"
  Base = -> Cut063
  Placement = pos=(0,58,0) rot=(0,0,1;0rad)
  Tool = -> Box044
FEATURE [Part::Box] Box045  label="Cube041"
  AttacherType = Attacher::AttachEngine3D
  Height = 80
  Length = 10
  Placement = pos=(-5,-5,16) rot=(0,0,1;0rad)
  Width = 10
FEATURE [Part::Wedge] Wedge004
  AttacherType = Attacher::AttachEngine3D
  Placement = pos=(-5,-5,16) rot=(-1,0,0;1.5708rad)
  X2max = 18
  X2min = 2
  Xmax = 20
  Xmin = 0
  Ymax = 14
  Ymin = 0
  Z2max = 8
  Z2min = 2
  Zmax = 10
  Zmin = 0
FEATURE [Part::Cylinder] Cylinder044  label="Cylinder016"
  Angle = 360
  AttacherType = Attacher::AttachEngine3D
  Height = 2
  Radius = 9.5
FEATURE [Part::Fuse] Fusion032
  Base = -> Box045
  Tool = -> Wedge004
FEATURE [Part::Fuse] Fusion033
  Base = -> Cylinder044
  Tool = -> Fusion032
FEATURE [Part::Box] Box046  label="Cube042"
  AttacherType = Attacher::AttachEngine3D
  Height = 2
  Length = 20
  Placement = pos=(0,-9.5,0) rot=(0,0,1;0rad)
  Width = 19
FEATURE [Part::Fuse] Fusion034
  Base = -> Fusion033
  Tool = -> Box046
FEATURE [Part::Fillet] Fillet017
  Base = -> Fusion034
  Edges = 3 edges r=3: [Edge9,Edge20,Edge24]
FEATURE [Part::Fillet] Fillet018
  Base = -> Fillet017
  Edges = 3 edges r=3: [Edge8,Edge27,Edge29]
FEATURE [Part::Fillet] Fillet019  label="piston002"
  Base = -> Fillet018
  Edges = 3 edges r=3: [Edge33,Edge34,Edge36]
  Placement = pos=(0,0,105) rot=(0,0,1;1.5708rad)
FEATURE [Part::Box] Box047  label="Cube043"
  AttacherType = Attacher::AttachEngine3D
  Height = 20
  Length = 26
  Placement = pos=(-13,-10,90) rot=(0,0,1;0rad)
  Width = 20
FEATURE [Part::Fuse] Fusion035
  Base = -> Cut059
  Tool = -> Box047
FEATURE [Part::Cut] Cut064  label="paste-extruder-drive-blockab"
  Base = -> Fusion035
  Placement = pos=(0,0,-37) rot=(0,0,1;0rad)
  Tool = -> Fillet019
FEATURE [App::DocumentObjectGroup] Group004  label="scratch"
  Group = -> [Cut034,Common,Common001,Cut013,Cut064]
FEATURE [Part::Chamfer] Chamfer002
  Base = -> Cut064
  Edges = 1 edges r=3: [Edge12]
FEATURE [Part::Chamfer] Chamfer003  label="paste-extruder-drive-block"
  Base = -> Chamfer002
  Edges = 1 edges r=3: [Edge6]
FEATURE [Part::Cylinder] Cylinder045  label="Cylinder017"
  Angle = 360
  AttacherType = Attacher::AttachEngine3D
  Height = 30
  Placement = pos=(0,0,-10) rot=(0,0,1;0rad)
  Radius = 2.7
FEATURE [Part::Box] Box048  label="Cube044"
  AttacherType = Attacher::AttachEngine3D
  Height = 35
  Length = 10
  Placement = pos=(-5,2,-12) rot=(0,0,1;0rad)
  Width = 10
FEATURE [Part::Cut] Cut065  label="NEMA17-shaft"
  Base = -> Cylinder045
  Tool = -> Box048
FEATURE [Part::Feature] Part__Feature005  label="paste-extruder-drive-gear001"
  Placement = pos=(0,0,3) rot=(0,0,1;0rad)
  shape: bbox 23.85 x 24.02 x 8 mm, 389 faces (baked)
FEATURE [Part::Cut] Cut066  label="smaller-drive-gear"
  Base = -> Part__Feature005
  Tool = -> Cut065
FEATURE [Part::Cylinder] Cylinder046  label="Cylinder018"
  Angle = 360
  AttacherType = Attacher::AttachEngine3D
  Height = 30
  Placement = pos=(22,0,-14) rot=(0,0,1;0rad)
  Radius = 3.2
FEATURE [Part::Cylinder] Cylinder047  label="Cylinder019"
  Angle = 360
  AttacherType = Attacher::AttachEngine3D
  Height = 30
  Placement = pos=(22,0,-26) rot=(0,0,1;0rad)
  Radius = 5.2
FEATURE [Part::Cylinder] Cylinder048  label="Cylinder020"
  Angle = 360
  AttacherType = Attacher::AttachEngine3D
  Height = 30
  Placement = pos=(22,0,9) rot=(0,0,1;0rad)
  Radius = 7
FEATURE [Part::Box] Box049  label="Cube045"
  AttacherType = Attacher::AttachEngine3D
  Height = 47
  Length = 10
  Placement = pos=(7.8,-8,0) rot=(0,0,1;0rad)
  Width = 16
FEATURE [Part::Box] Box050  label="Cube046"
  AttacherType = Attacher::AttachEngine3D
  Height = 47
  Length = 10
  Placement = pos=(21.8282,-16.2976,0) rot=(0,0,1;1.0472rad)
  Width = 16
FEATURE [Part::Box] Box051  label="Cube047"
  AttacherType = Attacher::AttachEngine3D
  Height = 47
  Length = 10
  Placement = pos=(36.0282,-8.29756,0) rot=(0,0,1;2.0944rad)
  Width = 16
FEATURE [Part::Box] Box052  label="Cube048"
  AttacherType = Attacher::AttachEngine3D
  Height = 47
  Length = 10
  Placement = pos=(36.2,8,0) rot=(0,0,1;3.14159rad)
  Width = 16
FEATURE [Part::Box] Box053  label="Cube049"
  AttacherType = Attacher::AttachEngine3D
  Height = 47
  Length = 10
  Placement = pos=(7.9718,8.29756,0) rot=(0,0,-1;1.0472rad)
  Width = 16
FEATURE [Part::Box] Box054  label="Cube050"
  AttacherType = Attacher::AttachEngine3D
  Height = 47
  Length = 10
  Placement = pos=(22.1718,16.2976,0) rot=(0,0,1;4.18879rad)
  Width = 16
FEATURE [Part::Fuse] Fusion036
  Base = -> Box049
  Tool = -> Box050
FEATURE [Part::Fuse] Fusion037
  Base = -> Box054
  Tool = -> Fusion036
FEATURE [Part::Fuse] Fusion038
  Base = -> Box053
  Tool = -> Fusion037
FEATURE [Part::Fuse] Fusion039
  Base = -> Box052
  Tool = -> Fusion038
FEATURE [Part::Fuse] Fusion040
  Base = -> Box051
  Tool = -> Fusion039
FEATURE [Part::Cut] Cut067
  Base = -> Cylinder048
  Tool = -> Fusion040
FEATURE [Part::Fuse] Fusion041
  Base = -> Cylinder047
  Tool = -> Cut067
FEATURE [Part::Fuse] Fusion042  label="driven-gear-hole"
  Base = -> Cylinder046
  Tool = -> Fusion041
FEATURE [Part::Feature] Part__Feature006  label="paste-extruder-driven-gear-003"
  Placement = pos=(23.04,0,3) rot=(0,0,1;0rad)
  shape: bbox 24.04 x 24.12 x 13 mm, 290 faces (baked)
FEATURE [Part::Cut] Cut068  label="smaller-driven-gear"
  Base = -> Part__Feature006
  Tool = -> Fusion042
FEATURE [Part::Cylinder] Cylinder049
  Angle = 360
  AttacherType = Attacher::AttachEngine3D
  Height = 10
  Placement = pos=(0,0,-1) rot=(0,0,1;0rad)
  Radius = 12
FEATURE [Part::MultiCommon] Common004  label="paste-extruder-drive-gear"
  Placement = pos=(0,0,3) rot=(0,0,1;0rad)
  Shapes = -> [Part__Feature,Cylinder049]
FEATURE [Part::FeaturePython] InvoluteGear  # WARN: FeaturePython — macro-defined, semantics opaque (R4)
  Placement = pos=(0,0,6) rot=(0,0,1;0rad)
  backlash = 0
  beta = 0
  clearance = 0.25
  double_helix = false
  dw = 21.06
  head = 0
  height = 5
  module = 1.62
  numpoints = 6
  pressure_angle = 20
  reversed_backlash = false
  shift = 0
  simple = false
  teeth = 13
  undercut = false
FEATURE [Part::FeaturePython] InvoluteGear001  # WARN: FeaturePython — macro-defined, semantics opaque (R4)
  Placement = pos=(22,0,0) rot=(0,0,1;0rad)
  backlash = 0
  beta = 0
  clearance = 0.25
  double_helix = false
  dw = 21.06
  head = 0
  height = 13.5
  module = 1.62
  numpoints = 6
  pressure_angle = 20
  reversed_backlash = false
  shift = 0
  simple = false
  teeth = 13
  undercut = false
FEATURE [Part::Cone] Cone001
  Angle = 360
  AttacherType = Attacher::AttachEngine3D
  Height = 3
  Placement = pos=(0,0,3.1) rot=(0,0,1;0rad)
  Radius1 = 5
  Radius2 = 8
FEATURE [Part::Cone] Cone002
  Angle = 360
  AttacherType = Attacher::AttachEngine3D
  Height = 4
  Placement = pos=(22,0,0) rot=(0,0,1;0rad)
  Radius1 = 8
  Radius2 = 13
FEATURE [Part::Cylinder] Cylinder050
  Angle = 360
  AttacherType = Attacher::AttachEngine3D
  Height = 10
  Placement = pos=(22,0,4) rot=(0,0,1;0rad)
  Radius = 13
FEATURE [Part::MultiFuse] Fusion043
  Shapes = -> [Cone002,Cylinder050]
FEATURE [Part::MultiCommon] Common005
  Placement = pos=(0,0,0.5) rot=(0,0,1;0rad)
  Shapes = -> [InvoluteGear001,Fusion043]
FEATURE [Part::MultiFuse] Fusion044
  Shapes = -> [InvoluteGear,Cone001]
FEATURE [App::DocumentObjectGroup] Group006  label="legacy"
  Group = -> [Part__Feature001,Common004]
FEATURE [Part::Cylinder] Cylinder051
  Angle = 360
  AttacherType = Attacher::AttachEngine3D
  Height = 15
  Radius = 2.5
FEATURE [Part::Box] Box055  label="Cube051"
  AttacherType = Attacher::AttachEngine3D
  Height = 15
  Length = 10
  Placement = pos=(1.93,-5,4.7) rot=(0,0,1;0rad)
  Width = 10
FEATURE [Part::Cut] Cut069
  Base = -> Cylinder051
  Tool = -> Box055
FEATURE [Part::Cut] Cut070
  Base = -> Fusion044
  Tool = -> Cut069
FEATURE [Part::Chamfer] Chamfer004  label="drive-gear"
  Base = -> Cut070
  Edges = 4 edges r=0.5: [Edge162,Edge163,Edge241,Edge243]
FEATURE [Part::Cylinder] Cylinder052
  Angle = 360
  AttacherType = Attacher::AttachEngine3D
  Height = 4.5
  Placement = pos=(22,0,0) rot=(0,0,1;0rad)
  Radius = 5
FEATURE [Part::Cylinder] Cylinder053
  Angle = 360
  AttacherType = Attacher::AttachEngine3D
  Height = 20.5
  Placement = pos=(22,0,0) rot=(0,0,1;0rad)
  Radius = 3.2
FEATURE [Part::Feature] M5_Nut_Hole
  Placement = pos=(22,0,9.9) rot=(0,0,1;0rad)
  shape: bbox 9.469 x 8.2 x 4.2 mm, 8 faces (baked)
FEATURE [Part::MultiFuse] Fusion045
  Shapes = -> [Cylinder052,Cylinder053,M5_Nut_Hole]
FEATURE [Part::Cut] Cut071
  Base = -> Common005
  Tool = -> Fusion045
FEATURE [Part::Chamfer] Chamfer005
  Base = -> Cut071
  Edges = 6 edges r=0.5: [Edge163,Edge164,Edge165,Edge166,Edge167,Edge168]
FEATURE [Part::Chamfer] Chamfer006  label="driven-gear-1"
  Base = -> Chamfer005
  Edges = 1 edges r=0.5: [Edge269]
FEATURE [Part::FeaturePython] InvoluteGear002  # WARN: FeaturePython — macro-defined, semantics opaque (R4)
  Placement = pos=(22,0,0) rot=(0,0,1;0rad)
  backlash = 0
  beta = 0
  clearance = 0.25
  double_helix = false
  dw = 21.06
  head = 0
  height = 13.5
  module = 1.62
  numpoints = 6
  pressure_angle = 20
  reversed_backlash = false
  shift = 0
  simple = false
  teeth = 13
  undercut = false
FEATURE [Part::Cone] Cone003
  Angle = 360
  AttacherType = Attacher::AttachEngine3D
  Height = 4
  Placement = pos=(22,0,0) rot=(0,0,1;0rad)
  Radius1 = 8
  Radius2 = 13
FEATURE [Part::Cylinder] Cylinder054
  Angle = 360
  AttacherType = Attacher::AttachEngine3D
  Height = 10
  Placement = pos=(22,0,4) rot=(0,0,1;0rad)
  Radius = 13
FEATURE [Part::MultiFuse] Fusion046
  Shapes = -> [Cone003,Cylinder054]
FEATURE [Part::MultiCommon] Common006
  Placement = pos=(0,0,0.5) rot=(0,0,1;0rad)
  Shapes = -> [InvoluteGear002,Fusion046]
FEATURE [Part::Cylinder] Cylinder055
  Angle = 360
  AttacherType = Attacher::AttachEngine3D
  Height = 4.5
  Placement = pos=(22,0,0) rot=(0,0,1;0rad)
  Radius = 5
FEATURE [Part::Cylinder] Cylinder056
  Angle = 360
  AttacherType = Attacher::AttachEngine3D
  Height = 20.5
  Placement = pos=(22,0,0) rot=(0,0,1;0rad)
  Radius = 3.2
FEATURE [Part::Feature] M5_Nut_Hole001
  Placement = pos=(22,0,10.3) rot=(0,0,1;0rad)
  shape: bbox 9.469 x 8.2 x 4.2 mm, 8 faces (baked)
FEATURE [Part::MultiFuse] Fusion047
  Shapes = -> [Cylinder055,Cylinder056,M5_Nut_Hole001]
FEATURE [Part::Cut] Cut072
  Base = -> Common006
  Tool = -> Fusion047
FEATURE [Part::Chamfer] Chamfer008
  Base = -> Cut072
  Edges = 6 edges r=0.5: [Edge163,Edge164,Edge165,Edge166,Edge167,Edge168]
FEATURE [Part::Chamfer] Chamfer007  label="driven-gear-2"
  Base = -> Chamfer008
  Edges = 1 edges r=0.5: [Edge269]
  Placement = pos=(-44,0,0) rot=(0,0,1;0rad)
FEATURE [App::DocumentObjectGroup] Group005  label="printed-parts"
  Group = -> [Cut043,Cut049,Fillet016,Clone,Common003,Cut062,Chamfer003,Chamfer004,Chamfer006,Chamfer007]
FEATURE [App::DocumentObjectGroup] Group  label="paste-extruder-parts"
  Group = -> [Group002,Group005]
